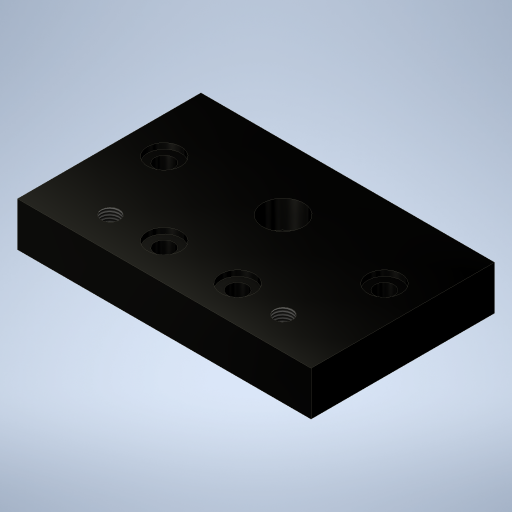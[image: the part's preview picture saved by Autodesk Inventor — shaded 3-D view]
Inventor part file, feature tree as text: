
AUTODESK INVENTOR PART (.ipt)
format: ipt  version: 2024.2 (Build 282272000, 272)  size: 297,984 bytes
history: native  units: mm
features: extrude x3, thread x2, hole x1
ambient origin geometry x8: Origin, YZ Plane, XZ Plane, XY Plane, X Axis, Y Axis, Z Axis, Center Point
bodies: Solid1 (feature_tree)
feature tree (6):
  extrude  "Extrusion1"  Depth=80.0mm
  extrude  "Extrusion2"  Depth=50.0mm
  thread  "Thread1"  [1 undecoded]
  thread  "Thread2"  [1 undecoded]
  extrude  "Extrusion3"  Depth=5.0mm
  hole  "Hole1"  [1 undecoded]
note: 3 required parameter values undecoded (feature->parameter linkage not recoverable at this tier; creation-order binding heuristic only, values carry confidence <= 0.55)
